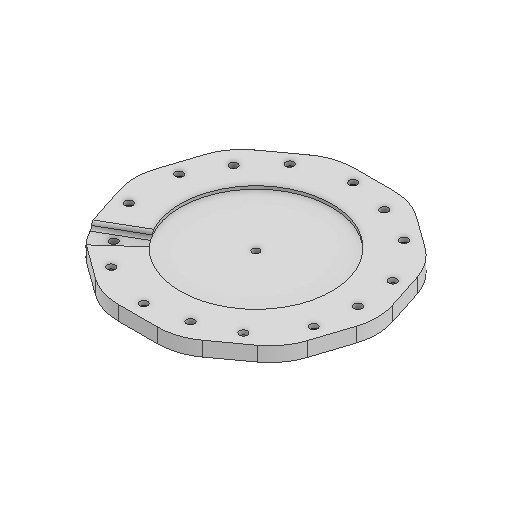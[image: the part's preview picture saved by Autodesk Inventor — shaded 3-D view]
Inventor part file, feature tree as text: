
AUTODESK INVENTOR PART (.ipt)
format: ipt  version: 2025 (Build 290162000, 162)  size: 332,800 bytes
history: native  units: mm
features: sketch x9, extrude x7, reference x5, other x3, fillet x2, pattern_circular x2, projected_geometry x2
ambient origin geometry x8: Origin, YZ Plane, XZ Plane, XY Plane, X Axis, Y Axis, Z Axis, Center Point
bodies: Solid1 (feature_tree)
feature tree (30):
  extrude  "Extrusion1"  Depth=5.0mm
  extrude  "Extrusion2"  Depth=10.0mm TaperAngle=0.0deg
  sketch  "Sketch3"  dims[d9=60.0mm d11=360.0deg d13=1.047198mm]
  extrude  "Extrusion3"  Depth=2.75mm
  fillet  "Fillet1"  Radius=2.75mm
  extrude  "Extrusion4"  Depth=1.047198mm
  extrude  "Extrusion5"  Depth=4.0mm TaperAngle=0.0deg
  extrude  "Extrusion6"  Depth=2.0mm
  pattern_circular  "Circular Pattern1"  [2 undecoded]
  fillet  "Fillet2"  Radius=7.0mm
  extrude  "Extrusion7"  Depth=40.0mm TaperAngle=360.0deg
  pattern_circular  "Circular Pattern2"  Count=4  [1 undecoded]
  sketch  "Sketch1"  dims[d0=104.0mm d1=5.0mm]
  sketch  "Sketch2"  dims[d6=38.1mm d7=69.85mm d8=2.75mm]
  projected_geometry  "Projected Loop1"
  projected_geometry  "Projected Loop2"
  sketch  "Sketch Circular Pattern1"  dims[d2=8.0mm d3=0.0mm d4=10.0mm d5=0.0mm]
  sketch  "Sketch4"  dims[d14=1.047198mm d15=4.0mm d16=0.0mm]
  reference  "Reference1"
  reference  "Reference2"
  sketch  "Sketch5"  dims[d17=2.0mm d18=8.5mm]
  sketch  "Sketch6"  dims[d19=4.0mm d20=0.0mm]
  reference  "Reference3"
  reference  "Reference4"
  sketch  "Sketch7"  dims[d21=0.0mm d22=0.0mm]
  sketch  "Sketch8"  dims[d23=8.0mm d24=8.0mm d25=7.0mm d26=0.0mm d27=50.0mm d28=360.0deg d30=40.0mm d31=70.0mm d32=5.5mm d33=0.0mm d34=0.0mm d35=50.0mm d36=360.0deg]
  reference  "Reference5"
  other  "<userpath>\Desktop\puppycat\liarAssembly.iam"
  other  "liarAssembly.iam"
  other  "lidarCageTop:1"
note: 3 required parameter values undecoded (feature->parameter linkage not recoverable at this tier; creation-order binding heuristic only, values carry confidence <= 0.55)
